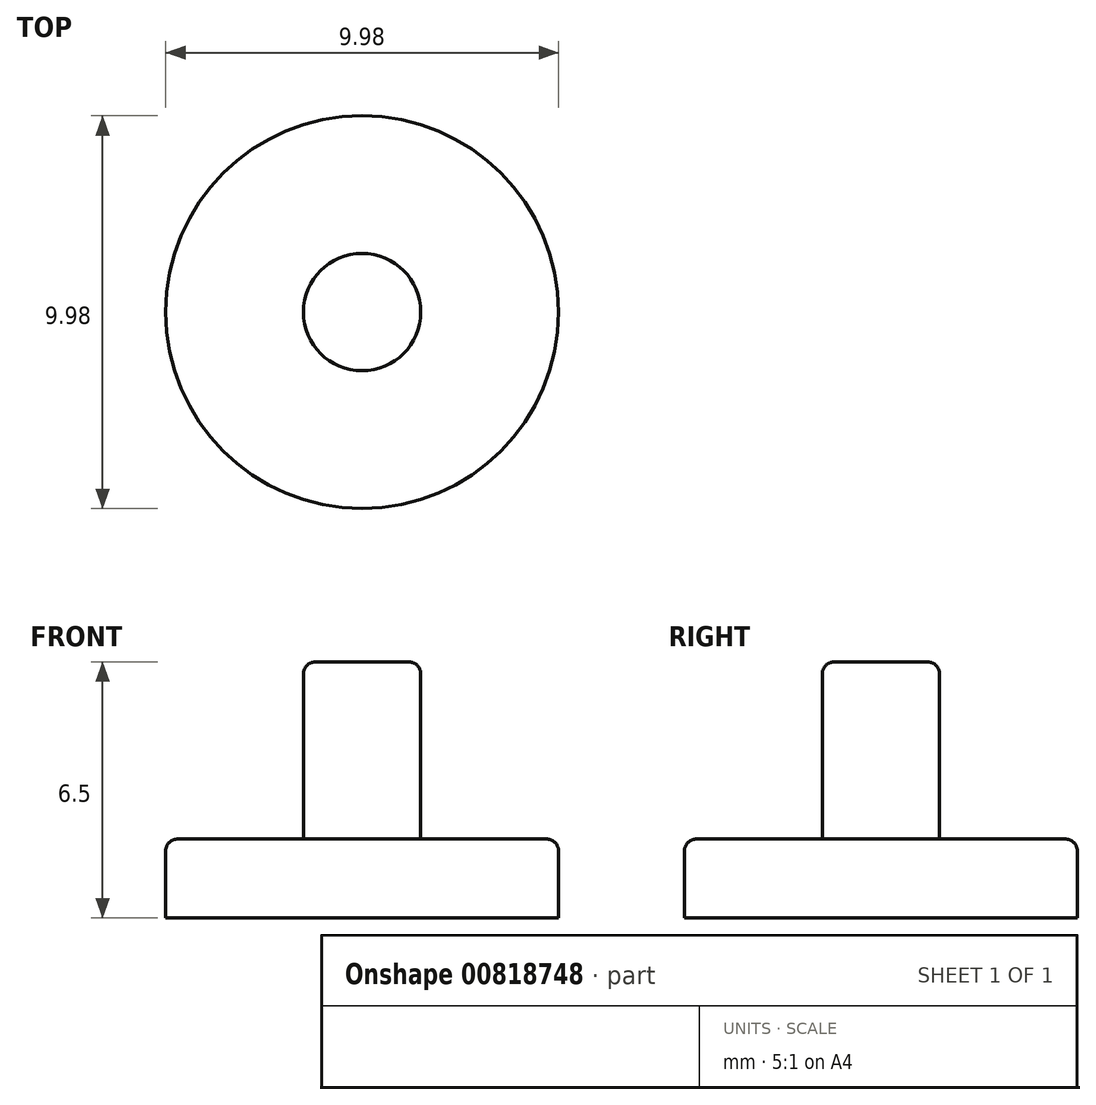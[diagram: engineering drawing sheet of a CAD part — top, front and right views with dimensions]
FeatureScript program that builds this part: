
annotation { "Feature Type Name" : "Feature", "Feature Type Description" : "" }
export const myFeature = defineFeature(function(context is Context, id is Id, definition is map)
    precondition{}
    {
        {
            var Q0;
            Q0=qCreatedBy(makeId("Top.planeOp"),FACE);
            var sketch = newSketch(context, id + "F0", { "sketchPlane" : qUnion([Q0])});
            skCircle(sketch, "E0", {"center": v(0, 0) * mm, "radius": 5 * mm});
            skSolve(sketch);
        }
        {
            var Q0;
            Q0=makeQuery(id+"F0.imprint","IMPRINT",FACE,{"disambiguationData":[TD([[makeQuery(id+"F0.imprint","IMPRINT",EDGE,{"derivedFrom":sQuery(id+"F0.wireOp",EDGE,"E0")}),1.0]])]});
            extrude(context, id + "F1", {"entities" : qUnion([Q0]), "depth" : 2 * mm, "offsetDistance" : 25 * mm});
        }
        {
            var Q0;
            Q0=makeQuery(id+"F1.opExtrude","CAP_FACE",FACE,{"disambiguationData":[OSD([sQuery(id+"F0.wireOp",EDGE,"E0")])],"isStart":false});
            var sketch = newSketch(context, id + "F2", { "sketchPlane" : qUnion([Q0])});
            skCircle(sketch, "E1", {"center": v(0, 0) * mm, "radius": 1.49 * mm});
            skSolve(sketch);
        }
        {
            var Q0;
            Q0=qSketchRegion(id+"F2",true);
            extrude(context, id + "F3", {"entities" : qUnion([Q0]), "operationType" : NewBodyOperationType.ADD, "depth" : 4.5 * mm, "offsetDistance" : 25 * mm});
        }
        {
            var Q0;
            Q0=makeQuery(id+"F3.opExtrude","CAP_FACE",FACE,{"disambiguationData":[OSD([sQuery(id+"F2.wireOp",EDGE,"E1")])],"isStart":false});
            var Q1;
            Q1=makeQuery(id+"F1.opExtrude","CAP_EDGE",EDGE,{"disambiguationData":[OSD([sQuery(id+"F0.wireOp",EDGE,"E0")])],"isStart":false});
            fillet(context, id + "F4", {"entities" : qUnion([Q0, Q1]), "radius" : .3 * mm, "tangentPropagation" : true, "allowEdgeOverflow" : false});
        }
    });
